# Revit family: Basketball_Backstop-Ceiling_Mount-Backward_Fold-IPIbyBison-IP1345BF
name_source: partatom
category: Specialty Equipment
units: mm (PartAtom-declared; Revit-internal decimal feet)

## family parameters
Always vertical = Yes
Cut with Voids When Loaded = No
Enable Cutting in Views = No
Maintain Annotation Orientation = No
OmniClass Number = 23.40.50.34.14
OmniClass Title = Gymnasium Equipment
Part Type = Normal
Room Calculation Point = No
Round Connector Dimension = Use Diameter
Shared = No

## types (1)
- Back Fold Rear Braced
    Available Options = as Specified
    Backboard Type = Backboard_BA42XLGlass
    CAD Details = https://www.arcat.com
    Default Elevation = 0' - 0"
    Description = Back Folding Basketball Frame and Backboard, Ceiling Mount
    Keynote = 11 66 00
    Manufacturer = IPI by Bison
    Model = IP1345BF
    Product Page URL = https://www.arcat.com
    Specification = https://www.arcat.com
    URL = https://ipibybison.com

## geometry (parser evidence)
native form markers: Sweep x9
no freeform markers — native parametric forms only
